# Revit family: Towel_Bar-American_Standard-Estate-77220XX_Series
name_source: partatom
category: Specialty Equipment
units: mm (PartAtom-declared; Revit-internal decimal feet)

## family parameters
Cut with Voids When Loaded = No
Host = Face
OmniClass Number = 23.40.20.21.27
OmniClass Title = Towel Bars
Part Type = Normal
Room Calculation Point = No
Round Connector Dimension = Use Diameter
Shared = Yes

## types (10) — shared parameters
Assembly Code = C1030220
Default Elevation = 56"
Height = 2 1/4"
Installation Type = Wall Mounted
Length = 3 7/8"
Manufacturer = American Standard
Product Documentation Link = https://lixil.cdn.celum.cloud
Product Page URL = https://www.americanstandard-us.com
Revised Date = 02/27/2024
URL = http://www.americanstandard-us.com
Warranty Information = Limited Lifetime Warranty

## per-type parameters (varying)
| type | Description | Finish | Material | W | Width |
| 7722024.002 | Estate Towel Bar | Metal-American Standard-002-Polished Chrome | Metal-American Standard-002-Polished Chrome | 24" | 26 1/4" |
| 7722018.002 | Estate® 18" Towel Bar | Metal-American Standard-002-Polished Chrome | Metal-American Standard-002-Polished Chrome | 18" | 20 1/4" |
| 7722018.278 | Estate® 18" Towel Bar | Metal-American Standard-278-Legacy Bronze | Metal-American Standard-278-Legacy Bronze | 18" | 20 1/4" |
| 7722018.295 | Estate® 18" Towel Bar | Metal-American Standard-295-Brushed Nickel | Metal-American Standard-295-Brushed Nickel | 18" | 20 1/4" |
| 7722018.013 | Estate® 18" Towel Bar | Metal-American Standard-013-Polished Nickel | Metal-American Standard-013-Polished Nickel | 18" | 20 1/4" |
| 7722024.295 | Estate Towel Bar | Metal-American Standard-295-Brushed Nickel | Metal-American Standard-295-Brushed Nickel | 24" | 26 1/4" |
| 7722024.243 | Estate Towel Bar | Metal-American Standard-295-Brushed Nickel | Metal-American Standard-295-Brushed Nickel | 24" | 26 1/4" |
| 7722024.278 | Estate Towel Bar | Metal-American Standard-295-Brushed Nickel | Metal-American Standard-295-Brushed Nickel | 24" | 26 1/4" |
| 7722024.013 | Estate Towel Bar | Metal-American Standard-013-Polished Nickel | Metal-American Standard-013-Polished Nickel | 24" | 26 1/4" |
| 7722018.243 | Estate® 18" Towel Bar | Metal-American Standard-243-Matte Black | Metal-American Standard-243-Matte Black | 18" | 20 1/4" |

note: column(s) folded — value = type name in every type: Model

## geometry (parser evidence)
native form markers: Sweep x3
no freeform markers — native parametric forms only
